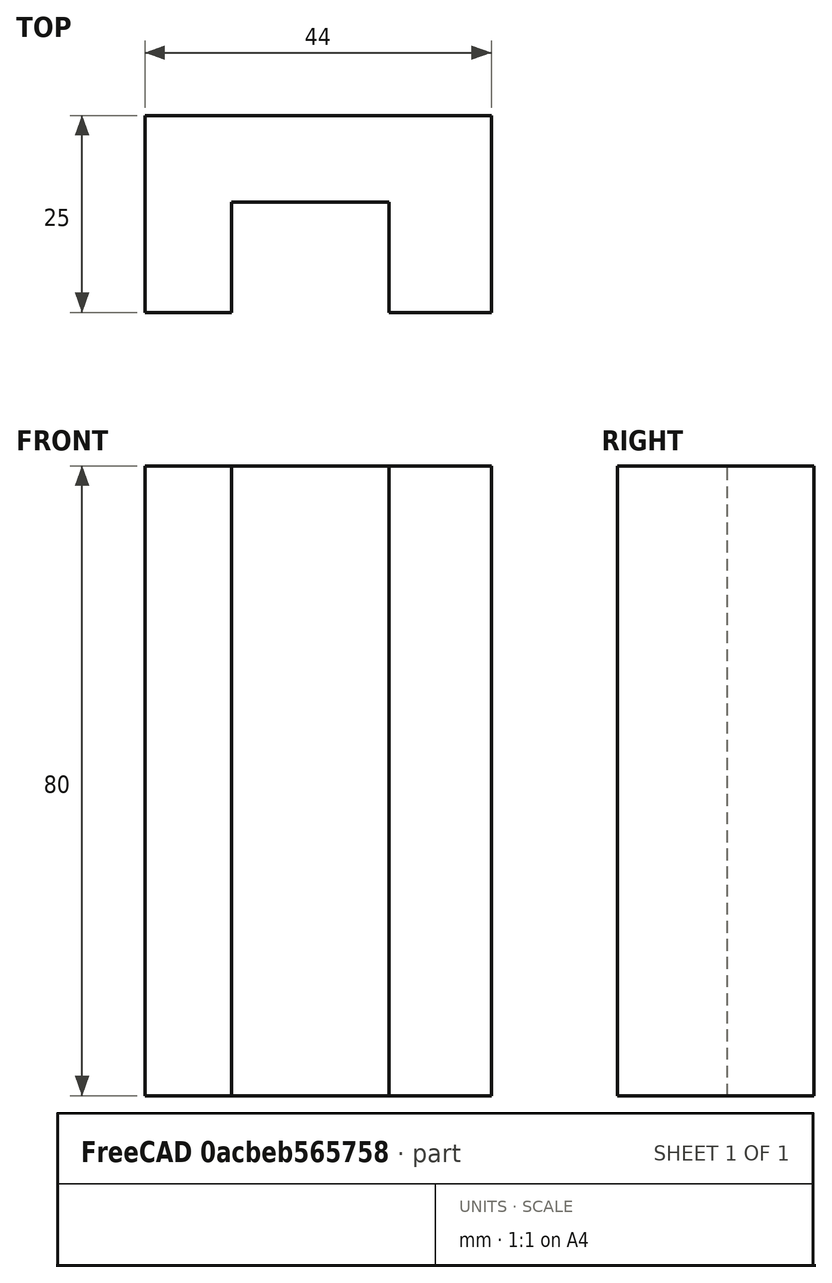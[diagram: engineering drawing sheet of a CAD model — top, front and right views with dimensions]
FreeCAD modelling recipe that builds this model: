
FCSTD DOCUMENT  (FreeCAD 0.21R33771 (Git))
Label: Pattino-20
License: All rights reserved
LicenseURL: http://en.wikipedia.org/wiki/All_rights_reserved
objects: Sketcher::SketchObject×2, PartDesign::CoordinateSystem×1, PartDesign::Pad×1, PartDesign::Body×1
note: 6 computed .brp shape members not serialized (recipe doc carries the construction recipe); baked Part::Feature solids carry a one-line shape summary decoded from their .brp

FEATURE [Sketcher::SketchObject] Sketch
  FullyConstrained = true
  MapMode = 5
  Support = -> [XY_Plane]
  sketch-geometry (8):
    g0: LineSegment StartX=0 StartY=0 StartZ=0 EndX=11 EndY=0 EndZ=0
    g1: LineSegment StartX=44 StartY=0 StartZ=0 EndX=44 EndY=25 EndZ=0
    g2: LineSegment StartX=44 StartY=25 StartZ=0 EndX=0 EndY=25 EndZ=0
    g3: LineSegment StartX=0 StartY=25 StartZ=0 EndX=0 EndY=0 EndZ=0
    g4: LineSegment StartX=11 StartY=0 StartZ=0 EndX=11 EndY=14 EndZ=0
    g5: LineSegment StartX=11 StartY=14 StartZ=0 EndX=31 EndY=14 EndZ=0
    g6: LineSegment StartX=31 StartY=14 StartZ=0 EndX=31 EndY=0 EndZ=0
    g7: LineSegment StartX=31 StartY=0 StartZ=0 EndX=44 EndY=0 EndZ=0
  constraints (22):
    c: Coincident(g7,g1)
    c: Coincident(g1,g2)
    c: Coincident(g2,g3)
    c: Coincident(g3,g0)
    c: Horizontal(g0)
    c: Horizontal(g2)
    c: Vertical(g1)
    c: Vertical(g3)
    c: Coincident(g0,g-1)
    c: DistanceY(g1,g1) = 25
    c: DistanceX(g2,g2) = 44
    c: Vertical(g4)
    c: Coincident(g5,g4)
    c: Horizontal(g5)
    c: Coincident(g6,g5)
    c: Vertical(g6)
    c: Coincident(g0,g4)
    c: Coincident(g7,g6)
    c: Tangent(g0,g7)
    c: DistanceX(g5,g5) = 20
    c: DistanceX(g0,g0) = 11
    c: DistanceY(g6,g6) = 14
FEATURE [Sketcher::SketchObject] Sketch002
  FullyConstrained = true
  MapMode = 5
  Placement = pos=(0,25,0) rot=(0,0.707107,0.707107;3.14159rad)
  sketch-geometry (8):
    g0: LineSegment StartX=-38 StartY=58 StartZ=0 EndX=-38 EndY=22 EndZ=0
    g1: LineSegment StartX=-38 StartY=22 StartZ=0 EndX=-6 EndY=22 EndZ=0
    g2: Circle CenterX=-38 CenterY=58 CenterZ=0 NormalX=0 NormalY=0 NormalZ=1 AngleXU=0 Radius=2.1
    g3: Circle CenterX=-38 CenterY=22 CenterZ=0 NormalX=0 NormalY=0 NormalZ=1 AngleXU=0 Radius=0
    g4: Circle CenterX=-6 CenterY=22 CenterZ=0 NormalX=0 NormalY=0 NormalZ=1 AngleXU=0 Radius=2.1
    g5: Circle CenterX=-6 CenterY=58 CenterZ=0 NormalX=0 NormalY=0 NormalZ=1 AngleXU=0 Radius=2.1
    g6: LineSegment StartX=-38 StartY=58 StartZ=0 EndX=-6 EndY=58 EndZ=0
    g7: Circle CenterX=-38 CenterY=22 CenterZ=0 NormalX=0 NormalY=0 NormalZ=1 AngleXU=0 Radius=2.1
  constraints (20):
    c: Vertical(g0)
    c: Coincident(g1,g0)
    c: Horizontal(g1)
    c: Coincident(g2,g0)
    c: Coincident(g3,g0)
    c: Tangent(g3,g1)
    c: Coincident(g4,g1)
    c: Coincident(g6,g0)
    c: Coincident(g6,g5)
    c: Coincident(g7,g0)
    c: Equal(g2,g7)
    c: Equal(g2,g5)
    c: Equal(g2,g4)
    c: Radius(g2) = 2.1
    c: Horizontal(g5,g0)
    c: DistanceY(g0,g0) = 36
    c: Equal(g6,g1)
    c: DistanceX(g1,g1) = 32
    c: DistanceX(g1,g-1) = 6
    c: DistanceY(g-1,g1) = 22
FEATURE [PartDesign::CoordinateSystem] LCS_Pattino_20
  AttacherType = Attacher::AttachEngine3D
  MapMode = 1
FEATURE [PartDesign::Pad] Pad
  Direction = (0,0,1)
  Length = 80
  Length2 = 10
  Profile = -> Sketch
  ReferenceAxis = -> Sketch [N_Axis]
  Type = 0
FEATURE [PartDesign::Body] Body
  Group = -> [Sketch,Sketch002,Pad,LCS_Pattino_20]
  Origin = -> Origin
  Tip = -> Pad
